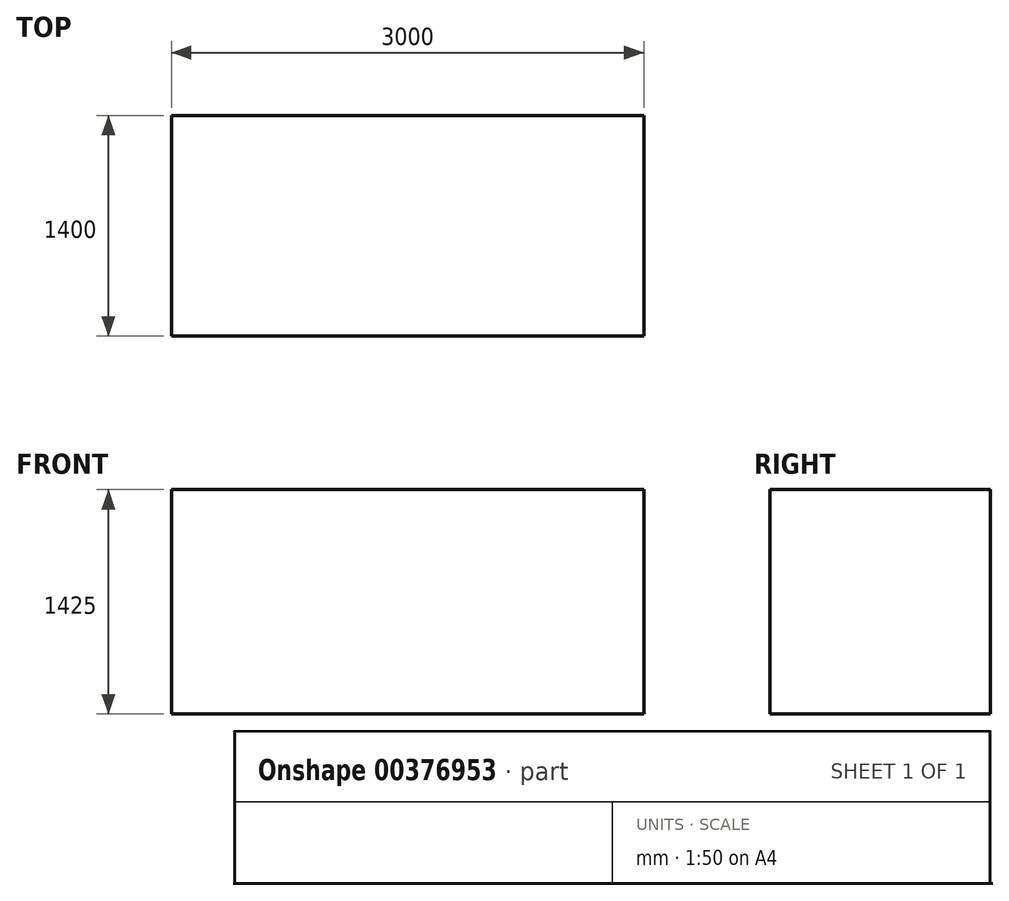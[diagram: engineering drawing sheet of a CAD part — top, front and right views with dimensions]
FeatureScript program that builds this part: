
annotation { "Feature Type Name" : "Feature", "Feature Type Description" : "" }
export const myFeature = defineFeature(function(context is Context, id is Id, definition is map)
    precondition{}
    {
        {
            var Q0;
            Q0=qCreatedBy(makeId("Top.planeOp"),FACE);
            var sketch = newSketch(context, id + "F0", { "sketchPlane" : qUnion([Q0])});
            skLineSegment(sketch, "E0.bottom", {"start": v(0, 0) * mm, "end": v(-1500, 0) * mm});
            skLineSegment(sketch, "E0.top", {"start": v(0, 700) * mm, "end": v(-1500, 700) * mm});
            skLineSegment(sketch, "E0.left", {"start": v(0, 0) * mm, "end": v(0, 700) * mm});
            skLineSegment(sketch, "E0.right", {"start": v(-1500, 0) * mm, "end": v(-1500, 700) * mm});
            skLineSegment(sketch, "E1.bottom", {"start": v(-1500, 700) * mm, "end": v(1500, 700) * mm});
            skLineSegment(sketch, "E1.top", {"start": v(-1500, -700) * mm, "end": v(1500, -700) * mm});
            skLineSegment(sketch, "E1.left", {"start": v(-1500, 700) * mm, "end": v(-1500, -700) * mm});
            skLineSegment(sketch, "E1.right", {"start": v(1500, 700) * mm, "end": v(1500, -700) * mm});
            skSolve(sketch);
        }
        {
            var Q0;
            {var subQ4=sQuery(id+"F0.wireOp",EDGE,"E0.bottom");Q0=makeQuery(id+"F0.imprint","IMPRINT",FACE,{"disambiguationData":[TD([[makeQuery(id+"F0.imprint","IMPRINT",EDGE,{"derivedFrom":subQ4}),1.0]])]});}
            var Q1;
            {var subQ0=sQuery(id+"F0.wireOp",EDGE,"E0.bottom");Q1=makeQuery(id+"F0.imprint","IMPRINT",FACE,{"disambiguationData":[TD([[makeQuery(id+"F0.imprint","IMPRINT",EDGE,{"derivedFrom":subQ0}),-1.0]])]});}
            extrude(context, id + "F1", {"entities" : qUnion([Q0, Q1]), "depth" : 1400 * mm});
        }
        {
            var Q0;
            Q0=makeQuery(id+"F1.opExtrude","CAP_FACE",FACE,{"disambiguationData":[OSD([sQuery(id+"F0.wireOp",EDGE,"E1.bottom"),sQuery(id+"F0.wireOp",EDGE,"E1.top"),sQuery(id+"F0.wireOp",EDGE,"E1.left"),sQuery(id+"F0.wireOp",EDGE,"E1.right")])],"isStart":true});
            extrude(context, id + "F2", {"entities" : qUnion([Q0]), "operationType" : NewBodyOperationType.ADD, "depth" : 25 * mm});
        }
    });
